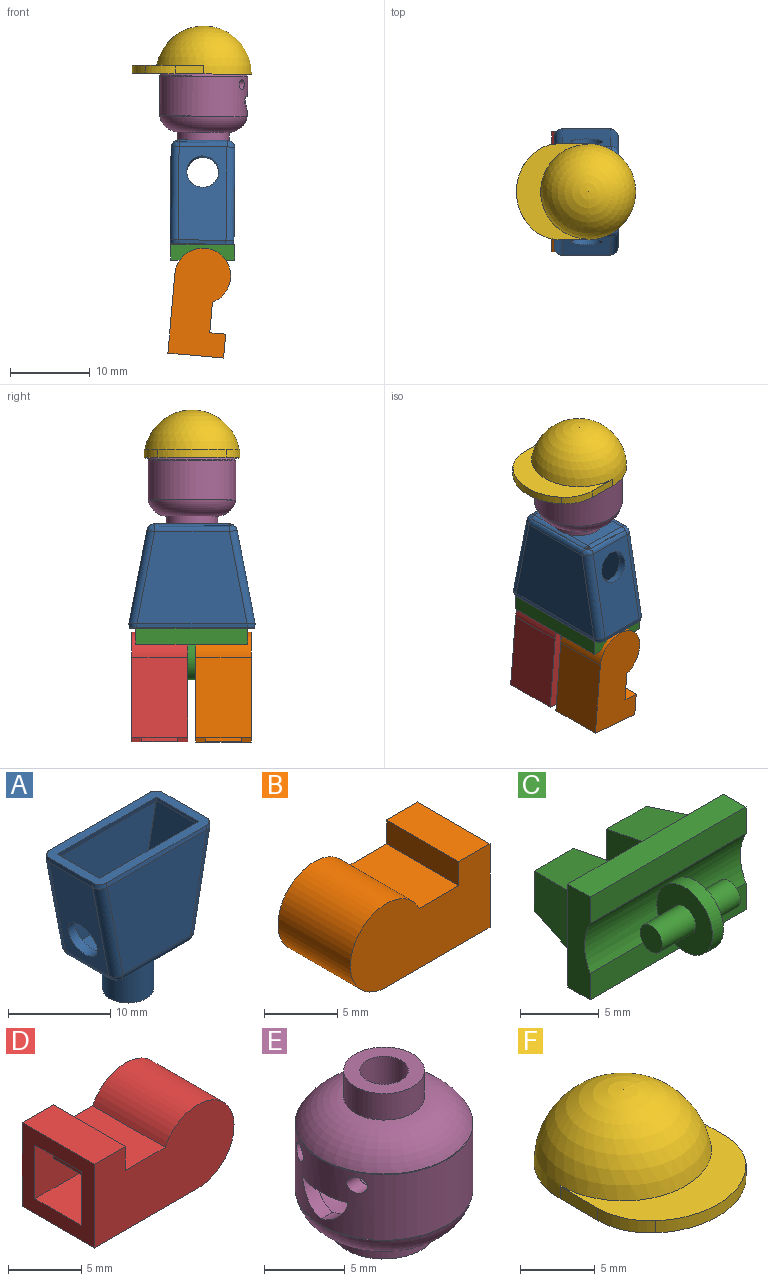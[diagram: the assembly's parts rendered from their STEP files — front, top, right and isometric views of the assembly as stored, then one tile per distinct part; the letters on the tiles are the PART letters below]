
ASSEMBLY  parts=6 mates=4
PART A: 40 faces, bbox 15.9x8x18 mm
  f0: plane 11.7x6mm, normal (0.98,0,-0.19), area 58.9mm2, adj f1,f36,f37,f38,f39
  f1: cylinder r=1mm len=6mm, axis (0,-1,0), area 8.3mm2, adj f0,f2,f31,f32,f35
  f2: sphere r=1mm, area 0.1mm2, adj f1,f3
  f3: cylinder r=1mm len=9.35mm, axis (-1,0,0), area 14.7mm2, adj f2,f4,f30,f31,f32
  f4: plane 13.78x11.52mm, normal (0,1,0), area 133.3mm2, adj f3,f5,f29,f38
  f5: plane 13.78x0.48mm, normal (0,0.99,0.17), area 6.6mm2, adj f4,f6,f7,f28
  f6: bspline ~1.03x1.01mm, area 0.7mm2, adj f5,f7,f37,f38
  f7: plane 15.69x7.88mm, normal (0,0,1), area 42.8mm2, adj f5,f6,f8,f21,f22,f23,f24,f25
  f8: plane 6x0.49mm, normal (-0.99,0,0.16), area 3mm2, adj f7,f9,f23,f28
  f9: plane 11.7x6mm, normal (-0.98,0,-0.19), area 58.9mm2, adj f8,f10,f14,f15,f29
  f10: cylinder r=1mm len=6mm, axis (0,-1,0), area 8.3mm2, adj f9,f11,f30,f32
  f11: sphere r=1mm, area 1mm2, adj f10,f12,f14
  f12: cylinder r=1mm len=9.35mm, axis (1,0,0), area 14.7mm2, adj f11,f13,f32,f35
  f13: plane 13.78x11.52mm, normal (0,-1,0), area 133.3mm2, adj f12,f14,f22,f36
  f14: cylinder r=1mm len=11.89mm, axis (0.19,0,-0.98), area 18.6mm2, adj f9,f11,f13,f23
  f15: cylinder r=2mm len=4.12mm, axis (-0.98,0,-0.19), area 12.6mm2, adj f9,f16
  f16: plane 11.52x6mm, normal (0.98,0,0.19), area 57.8mm2, adj f15,f17,f19,f20,f24,f26,f27
  f17: plane 13.75x11.44mm, normal (0,-1,0), area 132.1mm2, adj f16,f18,f19,f26
  f18: plane 11.52x6mm, normal (-0.98,0,0.19), area 57.8mm2, adj f17,f19,f20,f24,f25,f26,f39
  f19: plane 9.35x6mm, normal (0,0,1), area 56.1mm2, adj f16,f17,f18,f20
  f20: plane 13.75x11.44mm, normal (0,1,0), area 132.1mm2, adj f16,f18,f19,f24
  f21: bspline ~1.03x1.01mm, area 0.7mm2, adj f7,f22,f36,f37
  f22: plane 13.78x0.48mm, normal (0,-0.99,0.17), area 6.6mm2, adj f7,f13,f21,f23
  f23: bspline ~1.03x1.01mm, area 0.7mm2, adj f7,f8,f14,f22
  f24: plane 13.78x0.56mm, normal (0,0.99,-0.17), area 7.8mm2, adj f7,f16,f18,f20,f25,f27
  f25: plane 5.97x0.48mm, normal (-0.99,0,-0.16), area 2.8mm2, adj f7,f18,f24,f26
  f26: plane 13.78x0.56mm, normal (0,-0.99,-0.17), area 7.8mm2, adj f7,f16,f17,f18,f25,f27
  f27: plane 5.97x0.48mm, normal (0.99,0,-0.16), area 2.8mm2, adj f7,f16,f24,f26
  f28: bspline ~1.03x1.01mm, area 0.7mm2, adj f5,f7,f8,f29
  f29: cylinder r=1mm len=11.89mm, axis (-0.19,0,0.98), area 18.6mm2, adj f4,f9,f28,f30
  f30: sphere r=1mm, area 0.9mm2, adj f3,f10,f29
  f31: sphere r=1mm, area 0.5mm2, adj f1,f3,f38
  f32: plane 9.35x6mm, normal (0,0,-1), area 36.5mm2, adj f1,f3,f10,f12,f33
  f33: cylinder r=2.5mm len=5mm, axis (0,0,1), area 78.5mm2, adj f32,f34
  f34: plane 5x5mm, normal (0,0,-1), area 19.6mm2, adj f33
  f35: sphere r=1mm, area 1.4mm2, adj f1,f12,f36
  f36: cylinder r=1mm len=11.89mm, axis (-0.19,0,-0.98), area 18.6mm2, adj f0,f13,f21,f35
  f37: plane 6x0.49mm, normal (0.99,0,0.16), area 3mm2, adj f0,f6,f7,f21
  f38: cylinder r=1mm len=11.89mm, axis (0.19,0,0.98), area 18.6mm2, adj f0,f4,f6,f31
  f39: cylinder r=2mm len=4.12mm, axis (0.98,0,-0.19), area 12.6mm2, adj f0,f18
PART B: 17 faces, bbox 13.5x7x7 mm
  f0: plane 7x7mm, normal (1,0,0), area 28.8mm2, adj f4,f5,f6,f7,f10,f13,f14,f15
  f1: plane 7x2mm, normal (-1,0,0), area 14mm2, adj f2,f5,f6,f7
  f2: plane 7x3.84mm, normal (0,0,1), area 26.9mm2, adj f1,f3,f6,f7
  f3: cylinder r=3.5mm len=7mm, axis (0,1,0), area 104.6mm2, adj f2,f4,f6,f7
  f4: plane 10x7mm, normal (0,0,-1), area 70mm2, adj f0,f3,f6,f7
  f5: plane 7x3mm, normal (0,0,1), area 21mm2, adj f0,f1,f6,f7
  f6: plane 13.5x7mm, normal (0,-1,0), area 79.8mm2, adj f0,f1,f2,f3,f4,f5
  f7: plane 13.5x7mm, normal (0,1,0), area 76.6mm2, adj f0,f1,f2,f3,f4,f5,f8
  f8: cylinder r=1mm len=5mm, axis (0,1,0), area 31.4mm2, adj f7,f9
  f9: plane 2x2mm, normal (0,1,0), area 3.1mm2, adj f8
  f10: plane 10x4.5mm, normal (0,1,0), area 24mm2, adj f0,f11,f12,f13,f14,f16
  f11: plane 4.5x2mm, normal (1,0,0), area 9mm2, adj f10,f12,f14,f15
  f12: plane 6.01x4.5mm, normal (0,0,-1), area 27.1mm2, adj f10,f11,f15,f16
  f13: plane 10x4.5mm, normal (0,0,1), area 45mm2, adj f0,f10,f15,f16
  f14: plane 4.5x1.75mm, normal (0,0,-1), area 7.9mm2, adj f0,f10,f11,f15
  f15: plane 10x4.5mm, normal (0,-1,0), area 24mm2, adj f0,f11,f12,f13,f14,f16
  f16: cylinder r=2.25mm len=4.5mm, axis (0,1,0), area 17mm2, adj f10,f12,f13,f15
PART C: 25 faces, bbox 14x11.5x8 mm
  f0: plane 3.54x3.08mm, normal (0,1,0), area 10.9mm2, adj f1,f2,f19,f24
  f1: plane 5x4.5mm, normal (0,0.19,-0.98), area 20.5mm2, adj f0,f7,f19,f24
  f2: plane 5x4.5mm, normal (0,0.19,0.98), area 20.5mm2, adj f0,f7,f19,f24
  f3: plane 14x2mm, normal (0,0,-1), area 28mm2, adj f4,f6,f7,f10
  f4: plane 8x2mm, normal (1,0,0), area 14.7mm2, adj f3,f5,f7,f8,f9,f10
  f5: plane 14x2mm, normal (0,0,1), area 28mm2, adj f4,f6,f7,f9
  f6: plane 8x2mm, normal (-1,0,0), area 14.7mm2, adj f3,f5,f7,f8,f9,f10
  f7: plane 14x8mm, normal (0,1,0), area 67mm2, adj f1,f2,f3,f4,f5,f6,f18,f19
  f8: cylinder r=4mm len=14mm, axis (1,0,0), area 55.7mm2, adj f4,f6,f9,f10,f11,f12,f13
  f9: plane 14x2.06mm, normal (0,-1,0), area 28.9mm2, adj f4,f5,f6,f8
  f10: plane 14x2.06mm, normal (0,-1,0), area 28.9mm2, adj f3,f4,f6,f8
  f11: cylinder r=2.5mm len=5mm, axis (-1,0,0), area 14.8mm2, adj f8,f12,f13
  f12: plane 5x4.99mm, normal (1,0,0), area 16.5mm2, adj f8,f11,f16
  f13: plane 5x4.99mm, normal (-1,0,0), area 16.5mm2, adj f8,f11,f14
  f14: cylinder r=1mm len=3mm, axis (1,0,0), area 18.8mm2, adj f13,f15
  f15: plane 2x2mm, normal (-1,0,0), area 3.1mm2, adj f14
  f16: cylinder r=1mm len=3mm, axis (-1,0,0), area 18.8mm2, adj f12,f17
  f17: plane 2x2mm, normal (1,0,0), area 3.1mm2, adj f16
  f18: plane 5x4.5mm, normal (0,0.19,-0.98), area 20.5mm2, adj f7,f21,f22,f23
  f19: plane 5x5mm, normal (-0.98,0.19,0), area 20.6mm2, adj f0,f1,f2,f7
  f20: plane 5x4.5mm, normal (0,0.19,0.98), area 20.5mm2, adj f7,f21,f22,f23
  f21: plane 5x5mm, normal (0.98,0.19,0), area 20.6mm2, adj f7,f18,f20,f22
  f22: plane 3.54x3.08mm, normal (0,1,0), area 10.9mm2, adj f18,f20,f21,f23
  f23: plane 5x5mm, normal (-1,0,0), area 20.2mm2, adj f7,f18,f20,f22
  f24: plane 5x5mm, normal (1,0,0), area 20.2mm2, adj f0,f1,f2,f7
PART D: 17 faces, bbox 13.5x7x7 mm
  f0: plane 7x7mm, normal (-1,0,0), area 28.8mm2, adj f4,f5,f6,f7,f10,f13,f14,f15
  f1: plane 7x2mm, normal (1,0,0), area 14mm2, adj f2,f5,f6,f7
  f2: plane 7x3.84mm, normal (0,0,1), area 26.9mm2, adj f1,f3,f6,f7
  f3: cylinder r=3.5mm len=7mm, axis (0,1,0), area 104.6mm2, adj f2,f4,f6,f7
  f4: plane 10x7mm, normal (0,0,-1), area 70mm2, adj f0,f3,f6,f7
  f5: plane 7x3mm, normal (0,0,1), area 21mm2, adj f0,f1,f6,f7
  f6: plane 13.5x7mm, normal (0,-1,0), area 79.8mm2, adj f0,f1,f2,f3,f4,f5
  f7: plane 13.5x7mm, normal (0,1,0), area 76.6mm2, adj f0,f1,f2,f3,f4,f5,f8
  f8: cylinder r=1mm len=5mm, axis (0,1,0), area 31.4mm2, adj f7,f9
  f9: plane 2x2mm, normal (0,1,0), area 3.1mm2, adj f8
  f10: plane 10x4.5mm, normal (0,1,0), area 24mm2, adj f0,f11,f12,f13,f14,f16
  f11: plane 4.5x2mm, normal (-1,0,0), area 9mm2, adj f10,f12,f14,f15
  f12: plane 6.01x4.5mm, normal (0,0,-1), area 27.1mm2, adj f10,f11,f15,f16
  f13: plane 10x4.5mm, normal (0,0,1), area 45mm2, adj f0,f10,f15,f16
  f14: plane 4.5x1.75mm, normal (0,0,-1), area 7.9mm2, adj f0,f10,f11,f15
  f15: plane 10x4.5mm, normal (0,-1,0), area 24mm2, adj f0,f11,f12,f13,f14,f16
  f16: cylinder r=2.25mm len=4.5mm, axis (0,1,0), area 17mm2, adj f10,f12,f13,f15
PART E: 19 faces, bbox 12x12x12 mm
  f0: cylinder r=4.5mm len=9mm, axis (0,0,-1), area 132.8mm2, adj f4,f5,f14,f15,f16,f17,f18
  f1: cylinder r=5.5mm len=11mm, axis (0,0,-1), area 163.3mm2, adj f12,f13,f14,f15,f16,f17,f18
  f2: plane 5x5mm, normal (0,0,1), area 12.6mm2, adj f3,f11
  f3: cylinder r=1.5mm len=3mm, axis (0,0,-1), area 25.9mm2, adj f2,f4
  f4: torus R=1.77mm, axis (0,0,-1), area 65.7mm2, adj f0,f3
  f5: torus R=2.33mm, axis (0,0,-1), area 59.3mm2, adj f0,f6
  f6: cylinder r=2.25mm len=4.5mm, axis (0,0,-1), area 24.7mm2, adj f5,f7
  f7: plane 6.5x6.5mm, normal (0,0,-1), area 17.3mm2, adj f6,f8
  f8: cylinder r=3.25mm len=6.5mm, axis (0,0,-1), area 20.4mm2, adj f7,f9
  f9: torus R=3.05mm, axis (0,0,-1), area 92.9mm2, adj f8,f12
  f10: torus R=2.27mm, axis (0,0,-1), area 98.3mm2, adj f11,f13
  f11: cylinder r=2.5mm len=5mm, axis (0,0,-1), area 31.4mm2, adj f2,f10
  f12: torus R=5.4mm, axis (0,0,1), area 0.7mm2, adj f1,f9
  f13: torus R=5.4mm, axis (0,0,1), area 1.6mm2, adj f1,f10
  f14: cylinder r=0.6mm len=1.9mm, axis (1,0,0), area 4.4mm2, adj f0,f1
  f15: cylinder r=0.6mm len=1.9mm, axis (1,0,0), area 4.4mm2, adj f0,f1
  f16: plane 4x1.47mm, normal (0,0,-1), area 4.1mm2, adj f0,f1,f17,f18
  f17: cylinder r=2.5mm len=2mm, axis (1,0,0), area 3.1mm2, adj f0,f1,f16,f18
  f18: cylinder r=2.5mm len=2mm, axis (1,0,0), area 3.1mm2, adj f0,f1,f16,f17
PART F: 16 faces, bbox 12x15x6 mm
  f0: sphere r=5.5mm, area 142.1mm2, adj f1,f6,f15
  f1: plane 14.96x12mm, normal (0,0,-1), area 55.4mm2, adj f0,f2,f7,f8,f9,f10,f11,f15
  f2: sphere r=6mm, area 207.3mm2, adj f1,f12,f13,f14
  f3: sphere r=5.5mm, area 20.8mm2, adj f4
  f4: cylinder r=2.5mm len=5mm, axis (0,0,1), area 37.7mm2, adj f3,f5
  f5: plane 7x7mm, normal (0,0,-1), area 18.8mm2, adj f4,f6
  f6: cylinder r=3.5mm len=7mm, axis (0,0,1), area 38.3mm2, adj f0,f5
  f7: plane 3.59x1mm, normal (1,0,0), area 3.6mm2, adj f1,f8,f12,f13
  f8: cylinder r=5mm len=3.77mm, axis (0,0,-1), area 4.3mm2, adj f1,f7,f9,f12
  f9: cylinder r=6.52mm len=8.56mm, axis (0,0,-1), area 9.3mm2, adj f1,f8,f10,f12
  f10: cylinder r=5mm len=3.77mm, axis (0,0,-1), area 4.3mm2, adj f1,f9,f11,f12
  f11: plane 3.59x1mm, normal (-1,0,0), area 3.6mm2, adj f1,f10,f12,f14
  f12: plane 12x8.96mm, normal (0,0,1), area 38.8mm2, adj f2,f7,f8,f9,f10,f11,f13,f14
  f13: plane 1x0.08mm, normal (0,1,0), area 0mm2, adj f2,f7,f12
  f14: plane 1x0.08mm, normal (0,1,0), area 0mm2, adj f2,f11,f12
  f15: cylinder r=5.5mm len=11mm, axis (0,0,-1), area 4.5mm2, adj f0,f1
PLACE A rot(axis=(0.71,-0.71,0),179.6deg) t=(-14.28,1.95,28.07)mm
PLACE B rot(axis=(0,1,0),95deg) t=(-19.95,1.5,-53.11)mm
PLACE C rot(axis=(0.58,0.58,0.58),120deg) t=(-14.33,2,15.04)mm
PLACE D rot(axis=(-0.74,0,-0.68),180deg) t=(-19.95,2.5,-53.11)mm
PLACE E rot(axis=(0.01,0,1),177.7deg) t=(-14.22,1.95,34.07)mm
PLACE F rot(axis=(-0.01,0.01,-1),90deg) t=(-14.19,1.95,36.37)mm
MATE revolute D.f3 <-> C.f11  axis (0,-1,0) through (-14.33,2.5,11.05)mm
MATE revolute F.f4 <-> E.f0  axis (0.01,0,1) through (-14.15,1.95,40.07)mm
MATE revolute E.f0 <-> A.f33  axis (-0.01,0,-1) through (-14.28,1.95,28.07)mm
MATE revolute B.f3 <-> C.f11  axis (0,1,0) through (-14.33,1.5,11.05)mm
